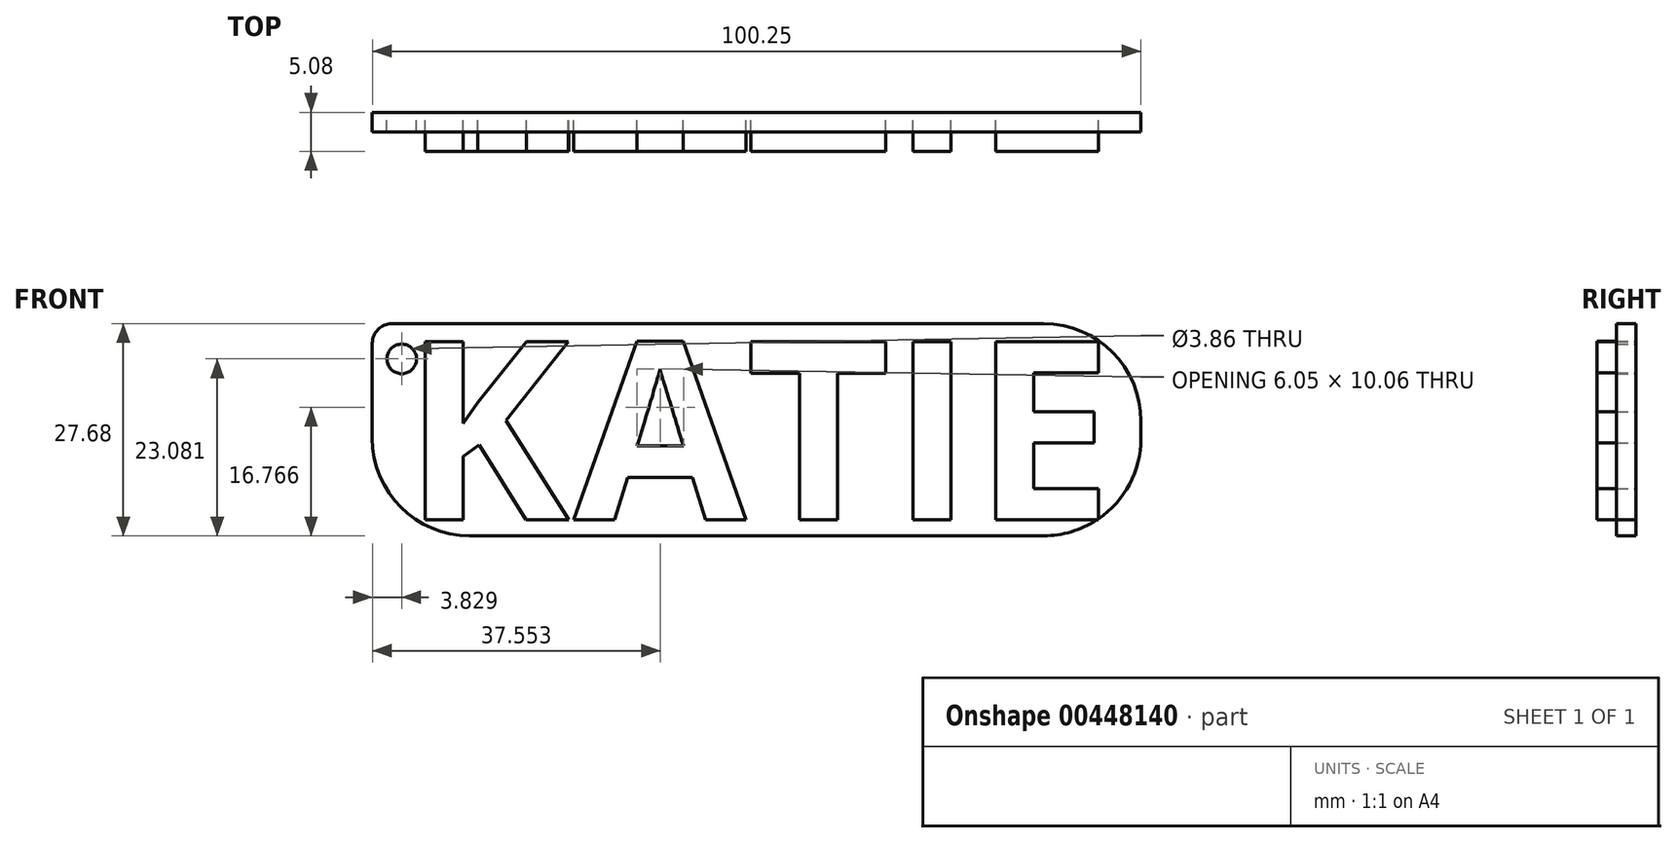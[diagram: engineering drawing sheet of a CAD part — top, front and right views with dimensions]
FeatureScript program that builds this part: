
annotation { "Feature Type Name" : "Feature", "Feature Type Description" : "" }
export const myFeature = defineFeature(function(context is Context, id is Id, definition is map)
    precondition{}
    {
        {
            var Q0;
            Q0=qCreatedBy(makeId("Front.planeOp"),FACE);
            var sketch = newSketch(context, id + "F0", { "sketchPlane" : qUnion([Q0])});
            skText(sketch, "E0", { "text": "KATIE", "fontName": "OpenSans-Bold.ttf"});
            const initialGuessF0  = {"E0": [-0.04017, 0.0182, 1, 0, 0.02344]};
            skSetInitialGuess(sketch, initialGuessF0);
            skSolve(sketch);
        }
        {
            var Q0;
            Q0 = qSketchRegion(id + "F0", true);
            var sketch = newSketch(context, id + "F1", { "sketchPlane" : qUnion([Q0])});
            skLineSegment(sketch, "E1.bottom", {"start": v(-44.15, 43.8) * mm, "end": v(56.1, 43.8) * mm});
            skLineSegment(sketch, "E1.top", {"start": v(-44.15, 16.13) * mm, "end": v(56.1, 16.13) * mm});
            skLineSegment(sketch, "E1.left", {"start": v(-44.15, 43.8) * mm, "end": v(-44.15, 16.13) * mm});
            skLineSegment(sketch, "E1.right", {"start": v(56.1, 43.8) * mm, "end": v(56.1, 16.13) * mm});
            skSolve(sketch);
        }
        {
            var Q0;
            Q0 = qSketchRegion(id + "F0", true);
            extrude(context, id + "F2", {"entities" : qUnion([Q0]), "depth" : 5.08 * mm});
        }
        {
            var Q0;
            Q0 = qSketchRegion(id + "F1", true);
            extrude(context, id + "F3", {"entities" : qUnion([Q0]), "depth" : 2.54 * mm});
        }
        {
            var Q0;
            Q0=makeQuery(id+"F3.opExtrude","SWEPT_EDGE",EDGE,{"disambiguationData":[OSD([sQuery(id+"F1.wireOp",EDGE,"E1.top"),sQuery(id+"F1.wireOp",EDGE,"E1.left")])]});
            var Q1;
            Q1=makeQuery(id+"F3.opExtrude","SWEPT_EDGE",EDGE,{"disambiguationData":[OSD([sQuery(id+"F1.wireOp",EDGE,"E1.bottom"),sQuery(id+"F1.wireOp",EDGE,"E1.right")])]});
            var Q2;
            Q2=makeQuery(id+"F3.opExtrude","SWEPT_EDGE",EDGE,{"disambiguationData":[OSD([sQuery(id+"F1.wireOp",EDGE,"E1.top"),sQuery(id+"F1.wireOp",EDGE,"E1.right")])]});
            fillet(context, id + "F4", {"entities" : qUnion([Q0, Q1, Q2]), "radius" : 12.7 * mm, "tangentPropagation" : true, "allowEdgeOverflow" : false});
        }
        {
            var Q0;
            Q0=makeQuery(id+"F3.opExtrude","SWEPT_EDGE",EDGE,{"disambiguationData":[OSD([sQuery(id+"F1.wireOp",EDGE,"E1.bottom"),sQuery(id+"F1.wireOp",EDGE,"E1.left")])]});
            fillet(context, id + "F5", {"entities" : qUnion([Q0]), "radius" : 2.54 * mm, "tangentPropagation" : true, "allowEdgeOverflow" : false});
        }
        {
            var Q0;
            Q0=qCreatedBy(makeId("Front.planeOp"),FACE);
            var sketch = newSketch(context, id + "F6", { "sketchPlane" : qUnion([Q0])});
            skCircle(sketch, "E2", {"center": v(-40.32, 39.21) * mm, "radius": 1.93 * mm});
            skPoint(sketch, "E2.first.point", {"position": v(-40.97, 41.03) * mm});
            skPoint(sketch, "E2.second.point", {"position": v(-41.9, 38.1) * mm});
            skPoint(sketch, "E2.third.point", {"position": v(-38.4, 39) * mm});
            skSolve(sketch);
        }
        {
            var Q0;
            Q0 = qSketchRegion(id + "F6", true);
            extrude(context, id + "F7", {"entities" : qUnion([Q0]), "operationType" : NewBodyOperationType.REMOVE, "depth" : 2.54 * mm});
        }
    });
